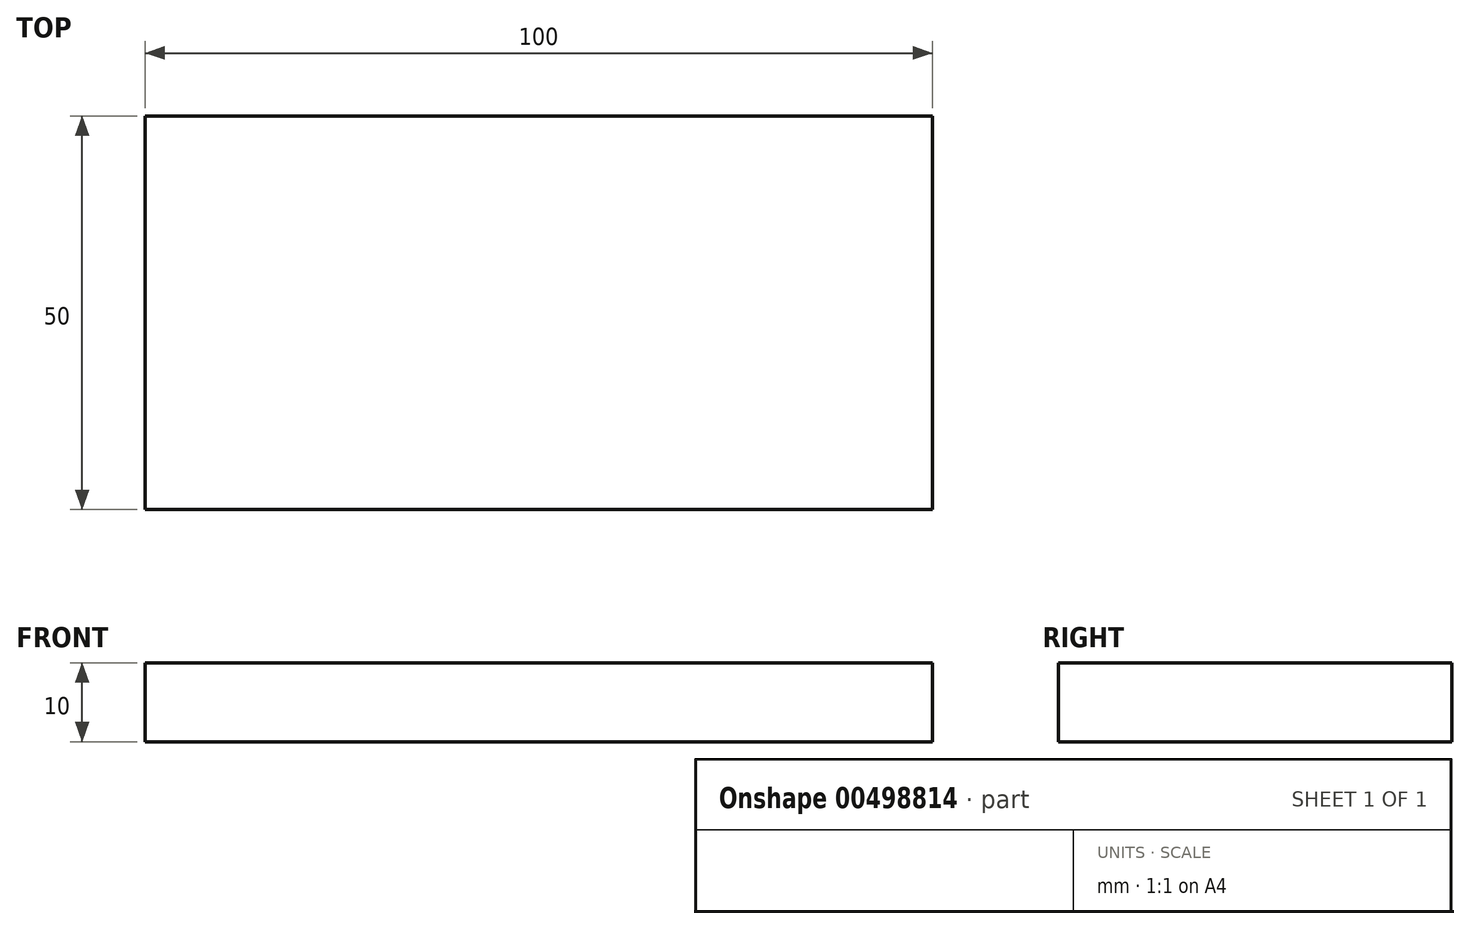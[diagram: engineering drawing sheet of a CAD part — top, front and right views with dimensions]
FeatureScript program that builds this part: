
annotation { "Feature Type Name" : "Feature", "Feature Type Description" : "" }
export const myFeature = defineFeature(function(context is Context, id is Id, definition is map)
    precondition{}
    {
        {
            var Q0;
            Q0=qCreatedBy(makeId("Top.planeOp"),FACE);
            var sketch = newSketch(context, id + "F0", { "sketchPlane" : qUnion([Q0])});
            skLineSegment(sketch, "E0.bottom", {"start": v(0, 0) * mm, "end": v(100, 0) * mm});
            skLineSegment(sketch, "E0.top", {"start": v(0, 50) * mm, "end": v(100, 50) * mm});
            skLineSegment(sketch, "E0.left", {"start": v(0, 0) * mm, "end": v(0, 50) * mm});
            skLineSegment(sketch, "E0.right", {"start": v(100, 0) * mm, "end": v(100, 50) * mm});
            skSolve(sketch);
        }
        {
            var Q0;
            Q0 = qSketchRegion(id + "F0", true);
            extrude(context, id + "F1", {"entities" : qUnion([Q0]), "depth" : 10 * mm});
        }
    });
